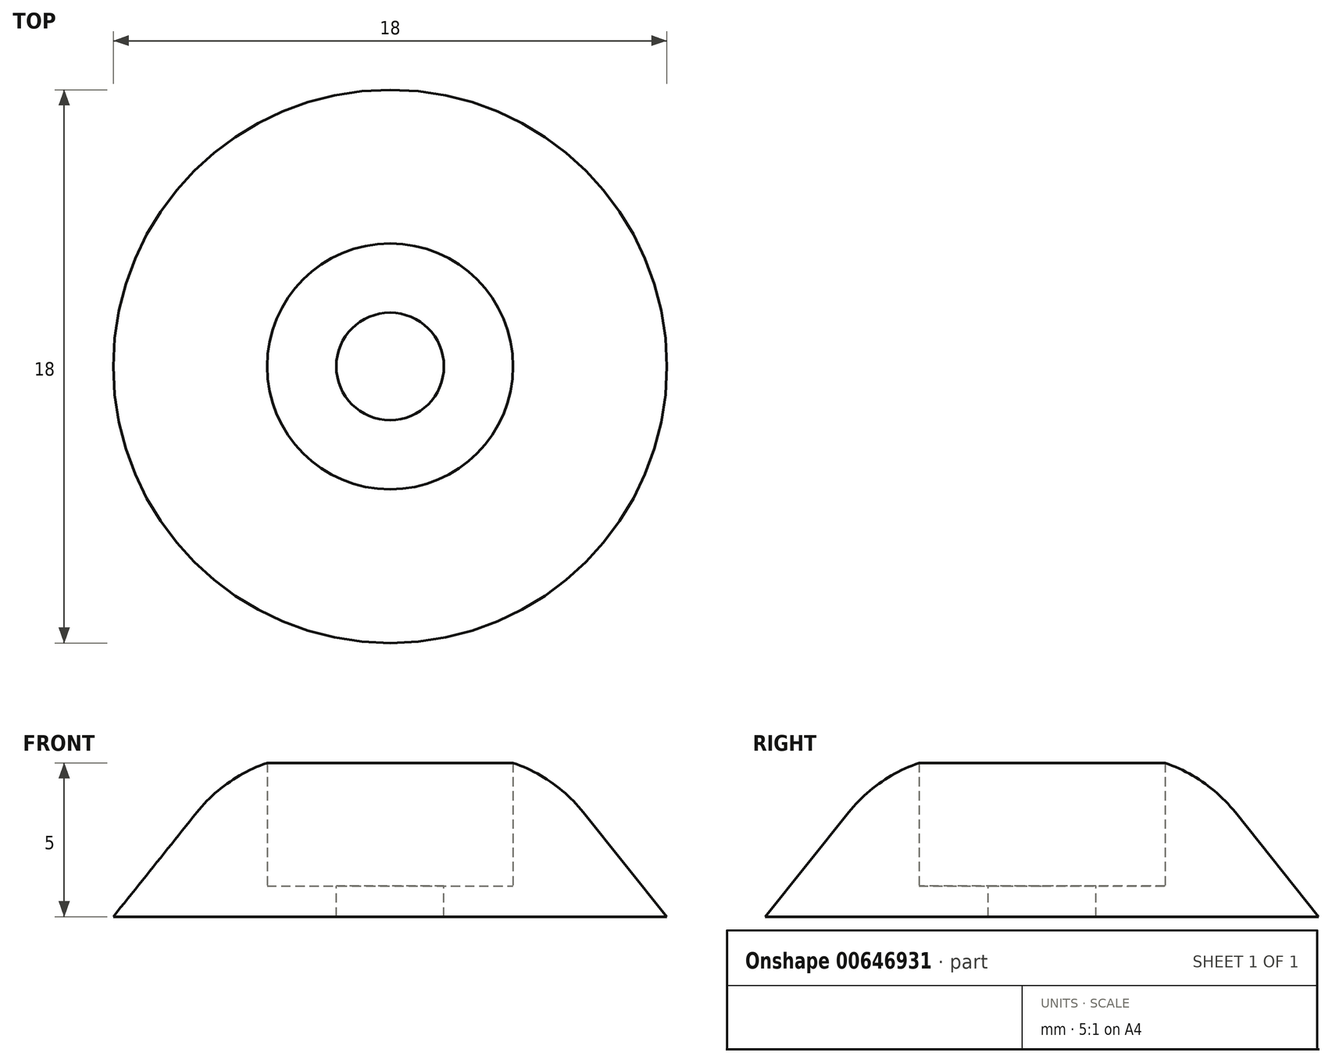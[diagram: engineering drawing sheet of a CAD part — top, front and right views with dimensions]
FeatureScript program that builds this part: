
annotation { "Feature Type Name" : "Feature", "Feature Type Description" : "" }
export const myFeature = defineFeature(function(context is Context, id is Id, definition is map)
    precondition{}
    {
        {
            var Q0;
            Q0=qCreatedBy(makeId("Front.planeOp"),FACE);
            var sketch = newSketch(context, id + "F0", { "sketchPlane" : qUnion([Q0])});
            skLineSegment(sketch, "E0", {"start": v(0, 0) * mm, "end": v(0, 5) * mm, "construction": true});
            skLineSegment(sketch, "E1", {"start": v(0, 5) * mm, "end": v(5, 5) * mm, "construction": true});
            skLineSegment(sketch, "E2", {"start": v(5, 5) * mm, "end": v(9, 0) * mm, "construction": true});
            skLineSegment(sketch, "E3", {"start": v(9, 0) * mm, "end": v(0, 0) * mm, "construction": true});
            skLineSegment(sketch, "E4", {"start": v(0, 0) * mm, "end": v(0, 1) * mm});
            skLineSegment(sketch, "E5", {"start": v(0, 1) * mm, "end": v(4, 1) * mm});
            skLineSegment(sketch, "E6", {"start": v(4, 1) * mm, "end": v(4, 5) * mm});
            skLineSegment(sketch, "E7", {"start": v(4, 5) * mm, "end": v(5, 5) * mm});
            skLineSegment(sketch, "E8", {"start": v(5, 5) * mm, "end": v(9, 0) * mm});
            skLineSegment(sketch, "E9", {"start": v(9, 0) * mm, "end": v(0, 0) * mm});
            skSolve(sketch);
        }
        {
            var Q0;
            Q0=makeQuery(id+"F0.imprint","IMPRINT",FACE,{"disambiguationData":[TD([[makeQuery(id+"F0.imprint","IMPRINT",EDGE,{"derivedFrom":sQuery(id+"F0.wireOp",EDGE,"E4")}),-1.0]])]});
            var Q1;
            Q1=sQuery(id+"F0.wireOp",EDGE,"E0");
            revolve(context, id + "F1", {"entities" : qUnion([Q0]), "axis" : qUnion([Q1]), "revolveType" : RevolveType.FULL});
        }
        {
            var Q0;
            Q0=makeQuery(id+"F1.opRevolve","SWEPT_FACE",FACE,{"disambiguationData":[OSD([sQuery(id+"F0.wireOp",EDGE,"E5")])]});
            var sketch = newSketch(context, id + "F2", { "sketchPlane" : qUnion([Q0])});
            skCircle(sketch, "E10", {"center": v(0, 0) * mm, "radius": 1.75 * mm});
            skSolve(sketch);
        }
        {
            var Q0;
            Q0=makeQuery(id+"F2.imprint","IMPRINT",FACE,{"disambiguationData":[TD([[makeQuery(id+"F2.imprint","IMPRINT",EDGE,{"derivedFrom":sQuery(id+"F2.wireOp",EDGE,"E10")}),1.0]])]});
            extrude(context, id + "F3", {"entities" : qUnion([Q0]), "operationType" : NewBodyOperationType.REMOVE, "endBound" : BoundingType.THROUGH_ALL, "oppositeDirection" : true, "depth" : 25 * mm, "offsetDistance" : 25 * mm});
        }
        {
            var Q0;
            Q0=makeQuery(id+"F1.opRevolve","SWEPT_EDGE",EDGE,{"disambiguationData":[OSD([sQuery(id+"F0.wireOp",EDGE,"E7"),sQuery(id+"F0.wireOp",EDGE,"E8")])]});
            fillet(context, id + "F4", {"entities" : qUnion([Q0]), "radius" : 5 * mm, "tangentPropagation" : true, "allowEdgeOverflow" : false});
        }
    });
